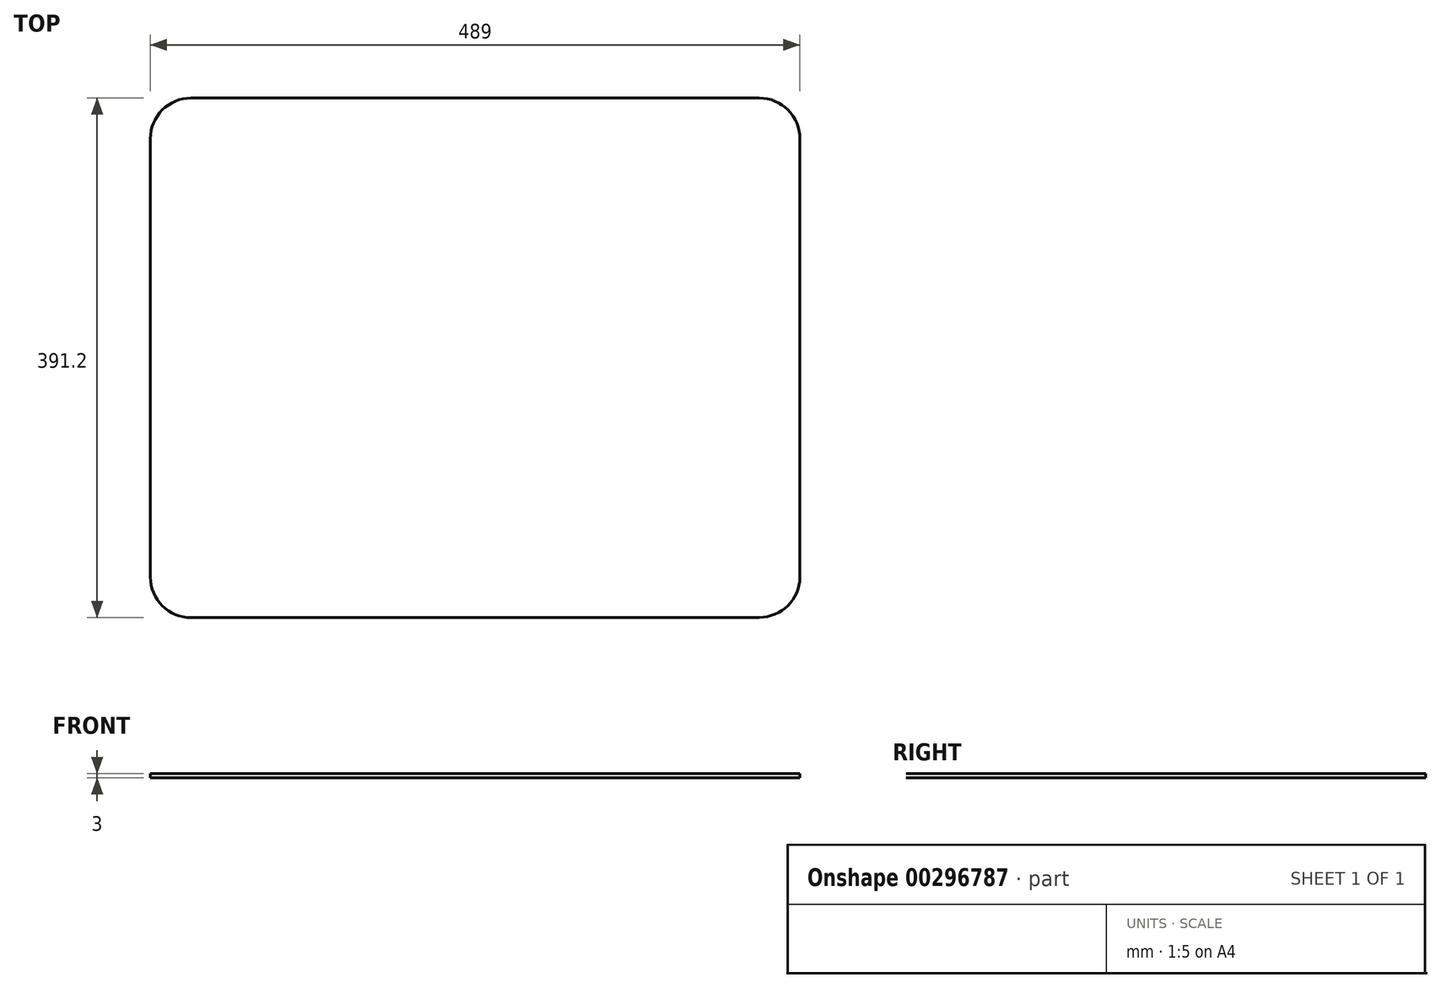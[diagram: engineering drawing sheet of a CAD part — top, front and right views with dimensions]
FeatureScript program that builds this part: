
annotation { "Feature Type Name" : "Feature", "Feature Type Description" : "" }
export const myFeature = defineFeature(function(context is Context, id is Id, definition is map)
    precondition{}
    {
        {
            var Q0;
            Q0=qCreatedBy(makeId("Top.planeOp"),FACE);
            var sketch = newSketch(context, id + "F0", { "sketchPlane" : qUnion([Q0])});
            skPoint(sketch, "E0.visualSharp", {"position": v(-311.84, 169.7) * mm});
            skPoint(sketch, "E1.visualSharp", {"position": v(183.16, 169.7) * mm});
            skPoint(sketch, "E2.visualSharp", {"position": v(183.16, -225.3) * mm});
            skPoint(sketch, "E3.visualSharp", {"position": v(-311.84, -225.3) * mm});
            skPoint(sketch, "E4.visualSharp", {"position": v(-261.84, 94.7) * mm});
            skPoint(sketch, "E5.visualSharp", {"position": v(133.16, 94.7) * mm});
            skPoint(sketch, "E6.visualSharp", {"position": v(133.16, -175.3) * mm});
            skPoint(sketch, "E7.visualSharp", {"position": v(-261.84, -175.3) * mm});
            skArc(sketch, "E8.0", {"start": v(-277.18, 166.7) * mm, "mid": v(-298.82, 157.73) * mm, "end": v(-307.78, 136.1) * mm});
            skLineSegment(sketch, "E8.1", {"start": v(-307.78, 136.1) * mm, "end": v(-307.78, -193.9) * mm});
            skLineSegment(sketch, "E8.2", {"start": v(-277.18, 166.7) * mm, "end": v(150.62, 166.7) * mm});
            skArc(sketch, "E8.3", {"start": v(-307.78, -193.9) * mm, "mid": v(-298.82, -215.54) * mm, "end": v(-277.18, -224.5) * mm});
            skArc(sketch, "E8.4", {"start": v(181.22, 136.1) * mm, "mid": v(172.26, 157.73) * mm, "end": v(150.62, 166.7) * mm});
            skLineSegment(sketch, "E8.5", {"start": v(181.22, -193.9) * mm, "end": v(181.22, 136.1) * mm});
            skArc(sketch, "E8.6", {"start": v(150.64, -224.36) * mm, "mid": v(172.21, -215.44) * mm, "end": v(181.22, -193.9) * mm});
            skLineSegment(sketch, "E8.7", {"start": v(-277.18, -224.5) * mm, "end": v(150.64, -224.36) * mm});
            skSolve(sketch);
        }
        {
            var Q0;
            Q0=makeQuery(id+"F0.imprint","IMPRINT",FACE,{"disambiguationData":[TD([[makeQuery(id+"F0.imprint","IMPRINT",EDGE,{"derivedFrom":sQuery(id+"F0.wireOp",EDGE,"E8.0")}),1.0]])]});
            extrude(context, id + "F1", {"entities" : qUnion([Q0]), "depth" : 3 * mm});
        }
    });
